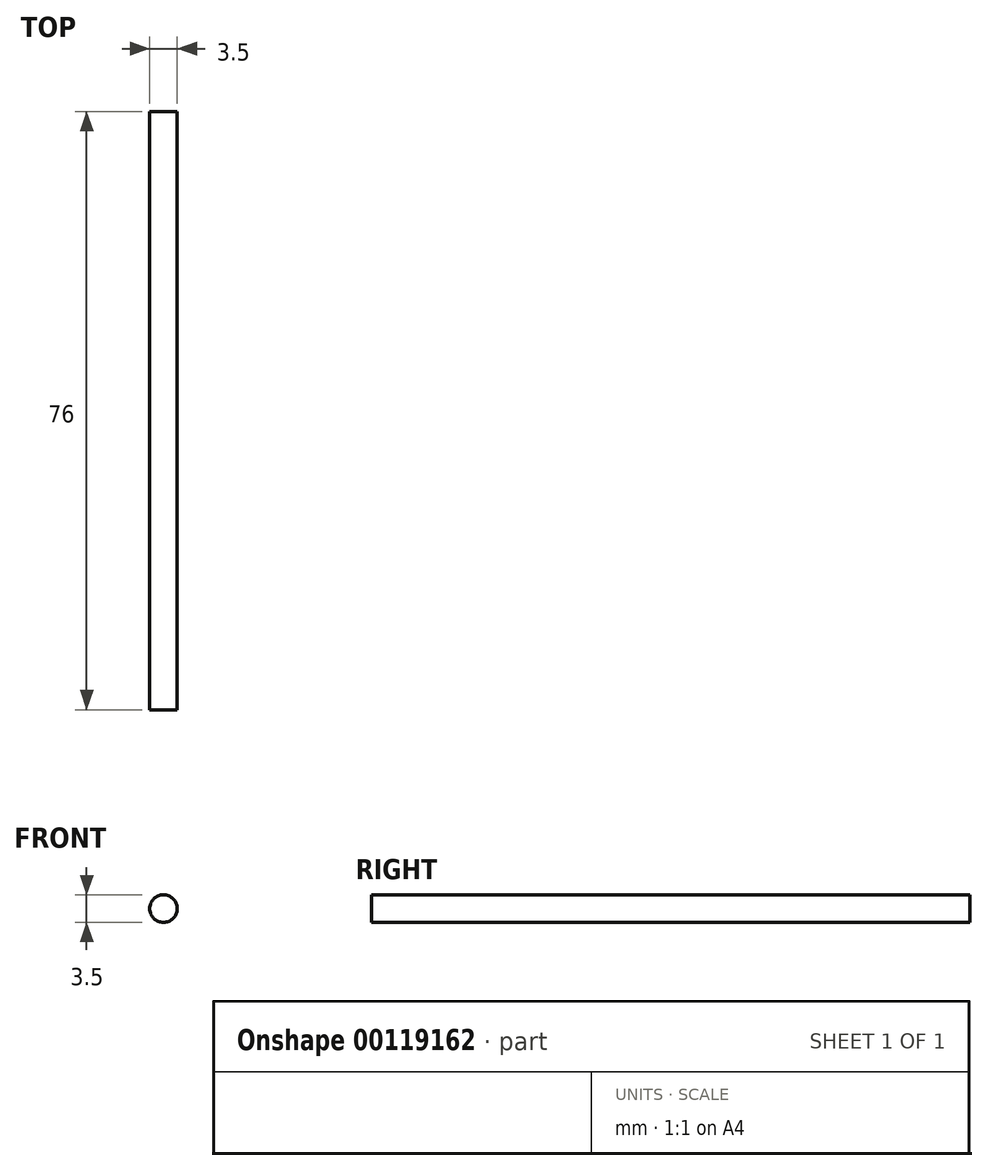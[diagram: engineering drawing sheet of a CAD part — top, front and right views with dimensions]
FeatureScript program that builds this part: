
annotation { "Feature Type Name" : "Feature", "Feature Type Description" : "" }
export const myFeature = defineFeature(function(context is Context, id is Id, definition is map)
    precondition{}
    {
        {
            var Q0;
            Q0=qCreatedBy(makeId("Front.planeOp"),FACE);
            var sketch = newSketch(context, id + "F0", { "sketchPlane" : qUnion([Q0])});
            skCircle(sketch, "E0", {"center": v(0, 0) * mm, "radius": 1.75 * mm});
            skSolve(sketch);
        }
        {
            var Q0;
            Q0=makeQuery(id+"F0.imprint","IMPRINT",FACE,{"disambiguationData":[TD([[makeQuery(id+"F0.imprint","IMPRINT",EDGE,{"derivedFrom":sQuery(id+"F0.wireOp",EDGE,"E0")}),1.0]])]});
            extrude(context, id + "F1", {"entities" : qUnion([Q0]), "depth" : 76 * mm});
        }
    });
